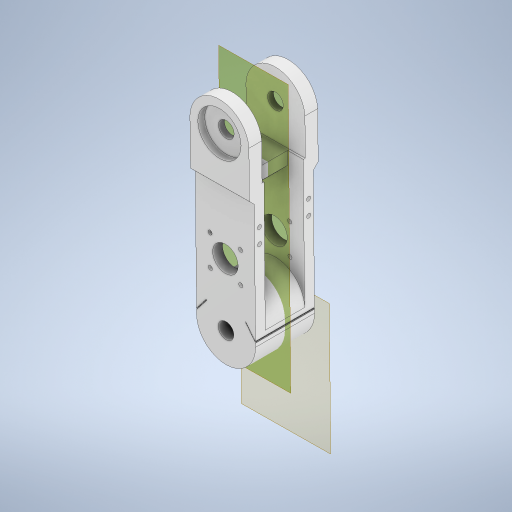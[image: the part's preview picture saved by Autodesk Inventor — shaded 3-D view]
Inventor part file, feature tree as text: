
AUTODESK INVENTOR PART (.ipt)
format: ipt  version: 2024 (Build 280153000, 153)  size: 1,913,856 bytes
history: native  units: mm
features: sketch x9, extrude x9, other x6, plane x5, mirror x4, chamfer x3, reference x3, fillet x1, projected_geometry x1
ambient origin geometry x8: Origin, YZ Plane, XZ Plane, XY Plane, X Axis, Y Axis, Z Axis, Center Point
bodies: Body1 (feature_tree)
feature tree (41):
  plane  "Work Plane3"
  sketch  "Sketch2"  dims[d4=60.0mm d5=140.0mm]
  plane  "Work Plane4"
  extrude  "Extrusion2"  Depth=60.0mm
  extrude  "Extrusion3"  Depth=30.0mm
  extrude  "Extrusion4"  TaperAngle=0.0deg  [1 undecoded]
  plane  "Work Plane7"
  mirror  "Mirror1"
  extrude  "Extrusion5"  Depth=60.0mm
  extrude  "Extrusion7"  Depth=8.0mm TaperAngle=0.0deg
  chamfer  "Chamfer6"  [1 undecoded]
  extrude  "Extrusion8"  Depth=16.0mm
  plane  "Work Plane8"
  mirror  "Mirror2"
  fillet  "Fillet1"  Radius=25.0mm
  plane  "Work Plane9"
  extrude  "Extrusion9"  TaperAngle=0.0deg  [1 undecoded]
  chamfer  "Chamfer7"  Distance=30.0mm Angle=45.0deg
  mirror  "Mirror3"
  chamfer  "Chamfer8"  Distance=26.0mm
  extrude  "Extrusion10"  TaperAngle=0.0deg  [1 undecoded]
  mirror  "Mirror4"
  extrude  "Extrusion11"  Depth=30.0mm
  sketch  "Sketch3"  dims[d6=60.0mm d7=30.0mm]
  reference  "Reference4"
  sketch  "Sketch5"  dims[d8=60.0mm d9=0.0mm d10=0.0mm d11=0.0mm]
  sketch  "Sketch6"  dims[d16=60.0mm d17=20.0mm]
  sketch  "Sketch8"  dims[d20=37.020508mm d21=8.0mm d22=0.0mm]
  sketch  "Sketch9"  dims[d32=10.0mm]
  reference  "Reference6"
  sketch  "Sketch10"  dims[d33=10.0mm]
  sketch  "Sketch11"  dims[d34=100.0mm d35=0.0mm d36=0.0mm]
  projected_geometry  "Projected Loop3"
  reference  "Reference7"
  sketch  "Sketch12"  dims[d43=16.0mm d44=16.0mm d45=25.0mm d46=0.0mm d47=0.0mm d54=12.0mm d55=30.0mm d56=45.0deg d57=26.0mm d58=0.0mm d59=0.0mm d60=30.0mm d62=5.0mm d63=0.0mm d64=5.0mm d65=2.0mm d66=45.0deg d67=5.0mm d68=2.0mm d69=45.0deg d70=14.0mm d71=7.0mm d72=0.0mm d73=16.0mm d77=5.0mm d78=4.2mm d79=5.0mm d80=15.0mm d81=12.0mm d82=0.0mm d83=0.0mm d84=4.2mm d85=45.04038mm d2=0.5mm d3=0.872665mm]
  other  "<userpath>\Documents\Inventor\robot arm\base.iam"
  other  "base.iam"
  other  "base:1"
  other  "stepper motor:1"
  other  "middel arm"
  other  "<userpath>\Documents\Inventor\robot arm\base.iam"
note: 4 required parameter values undecoded (feature->parameter linkage not recoverable at this tier; creation-order binding heuristic only, values carry confidence <= 0.55)
